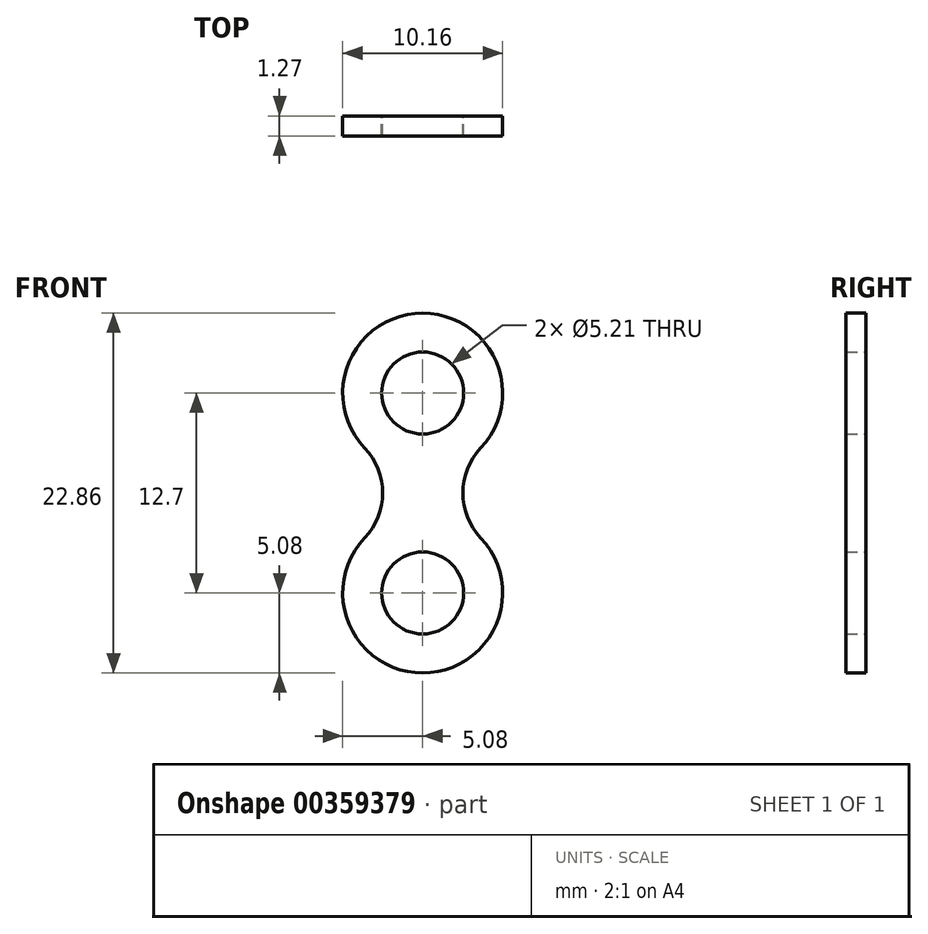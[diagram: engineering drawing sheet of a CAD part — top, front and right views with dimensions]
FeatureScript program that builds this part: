
annotation { "Feature Type Name" : "Feature", "Feature Type Description" : "" }
export const myFeature = defineFeature(function(context is Context, id is Id, definition is map)
    precondition{}
    {
        {
            var Q0;
            Q0=qCreatedBy(makeId("Front.planeOp"),FACE);
            var sketch = newSketch(context, id + "F0", { "sketchPlane" : qUnion([Q0])});
            skArc(sketch, "E0", {"start": v(3.69, -3.5) * mm, "mid": v(0, 5.08) * mm, "end": v(-3.69, -3.5) * mm});
            skArc(sketch, "E1", {"start": v(-3.69, -9.2) * mm, "mid": v(0, -17.78) * mm, "end": v(3.69, -9.2) * mm});
            skArc(sketch, "E2", {"start": v(-3.69, -9.2) * mm, "mid": v(-2.55, -6.35) * mm, "end": v(-3.69, -3.5) * mm});
            skArc(sketch, "E3", {"start": v(3.69, -3.5) * mm, "mid": v(2.55, -6.35) * mm, "end": v(3.69, -9.2) * mm});
            skCircle(sketch, "E4", {"center": v(0, 0) * mm, "radius": 2.6 * mm});
            skCircle(sketch, "E5", {"center": v(0, -12.7) * mm, "radius": 2.6 * mm});
            skSolve(sketch);
        }
        {
            var Q0;
            Q0=makeQuery(id+"F0.imprint","IMPRINT",FACE,{"disambiguationData":[TD([[makeQuery(id+"F0.imprint","IMPRINT",EDGE,{"derivedFrom":sQuery(id+"F0.wireOp",EDGE,"E0")}),1.0]])]});
            extrude(context, id + "F1", {"entities" : qUnion([Q0]), "depth" : 1.27 * mm});
        }
    });
